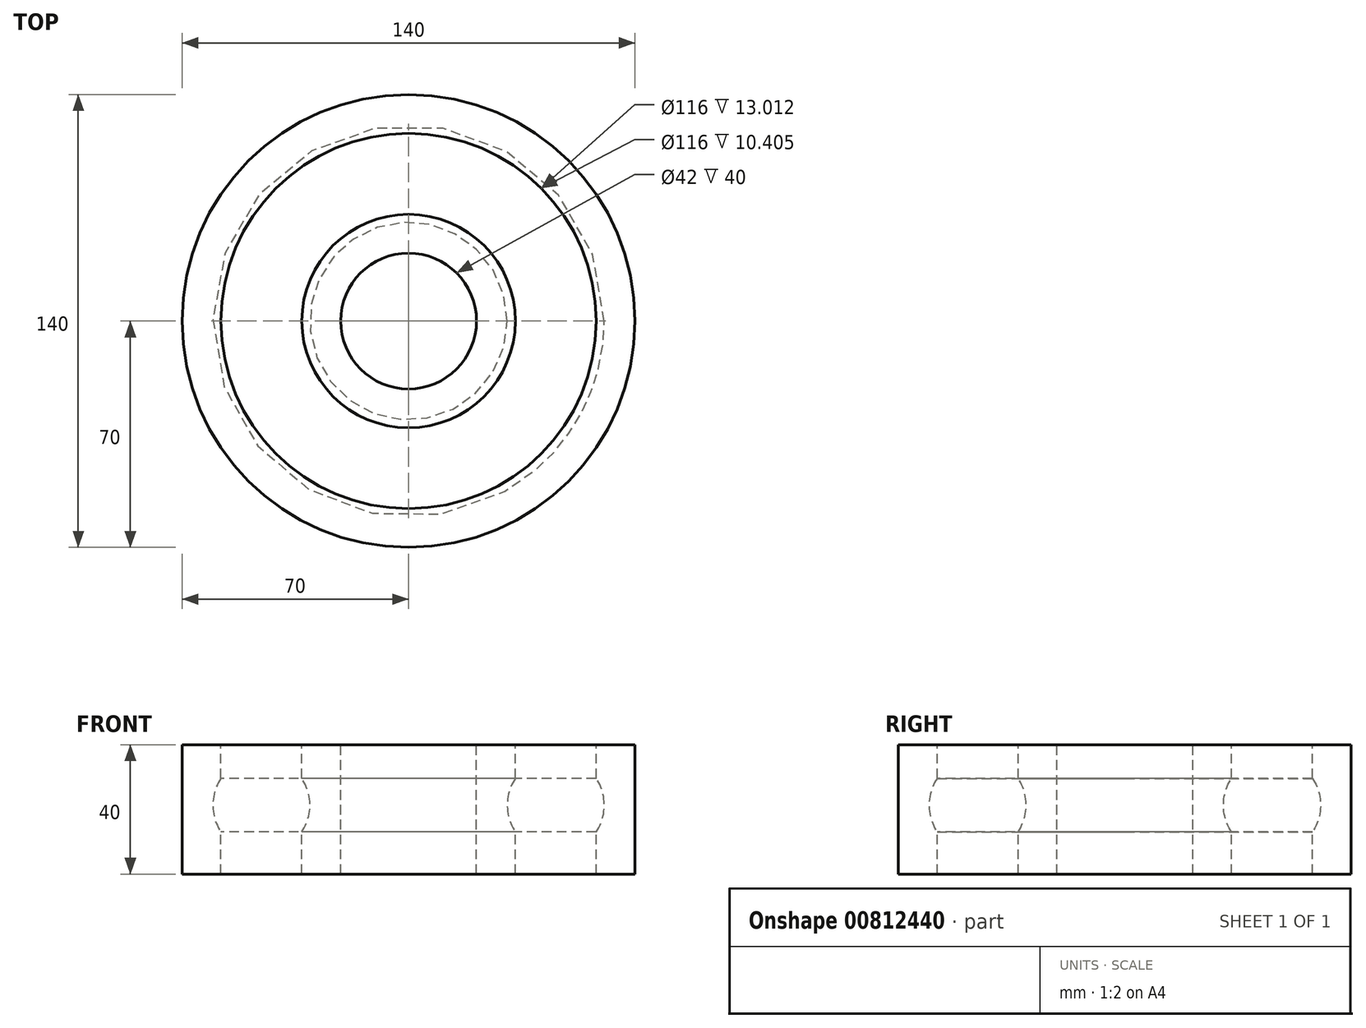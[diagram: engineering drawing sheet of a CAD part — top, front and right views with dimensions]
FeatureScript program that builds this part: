
annotation { "Feature Type Name" : "Feature", "Feature Type Description" : "" }
export const myFeature = defineFeature(function(context is Context, id is Id, definition is map)
    precondition{}
    {
        {
            var Q0;
            Q0=qCreatedBy(makeId("Front.planeOp"),FACE);
            var sketch = newSketch(context, id + "F0", { "sketchPlane" : qUnion([Q0])});
            skLineSegment(sketch, "E0.bottom", {"start": v(12.5, 17.69) * mm, "end": v(24.5, 17.69) * mm});
            skLineSegment(sketch, "E0.top", {"start": v(12.5, -22.31) * mm, "end": v(24.5, -22.31) * mm});
            skLineSegment(sketch, "E0.left", {"start": v(12.5, 17.69) * mm, "end": v(12.5, -22.31) * mm});
            skLineSegment(sketch, "E0.right", {"start": v(24.5, 17.69) * mm, "end": v(24.5, -22.31) * mm});
            skPoint(sketch, "E1.firstSnap0", {"position": v(18.5, 17.69) * mm});
            skLineSegment(sketch, "E1.bottom", {"start": v(-24.5, 17.69) * mm, "end": v(-12.5, 17.69) * mm});
            skLineSegment(sketch, "E1.top", {"start": v(-24.5, -22.31) * mm, "end": v(-12.5, -22.31) * mm});
            skLineSegment(sketch, "E1.left", {"start": v(-24.5, 17.69) * mm, "end": v(-24.5, -22.31) * mm});
            skLineSegment(sketch, "E1.right", {"start": v(-12.5, 17.69) * mm, "end": v(-12.5, -22.31) * mm});
            skCircle(sketch, "E2", {"center": v(0, -1.01) * mm, "radius": 15 * mm});
            skLineSegment(sketch, "E3", {"start": v(-45.5, 28.22) * mm, "end": v(-45.5, -36.2) * mm});
            skLineSegment(sketch, "E4", {"start": v(0, 26.4) * mm, "end": v(0, -22.77) * mm});
            skSolve(sketch);
        }
        {
            var Q0;
            {var subQ1=sQuery(id+"F0.wireOp",EDGE,"E1.bottom");Q0=makeQuery(id+"F0.imprint","IMPRINT",FACE,{"disambiguationData":[TD([[makeQuery(id+"F0.imprint","IMPRINT",EDGE,{"derivedFrom":subQ1}),-1.0]])]});}
            var Q1;
            {var subQ5=sQuery(id+"F0.wireOp",EDGE,"E0.bottom");Q1=makeQuery(id+"F0.imprint","IMPRINT",FACE,{"disambiguationData":[TD([[makeQuery(id+"F0.imprint","IMPRINT",EDGE,{"derivedFrom":subQ5}),-1.0]])]});}
            var Q2;
            Q2=sQuery(id+"F0.wireOp",EDGE,"E3");
            revolve(context, id + "F1", {"surfaceOperationType" : NewSurfaceOperationType.NEW, "entities" : qUnion([Q0, Q1]), "axis" : qUnion([Q2]), "revolveType" : RevolveType.FULL});
        }
    });
